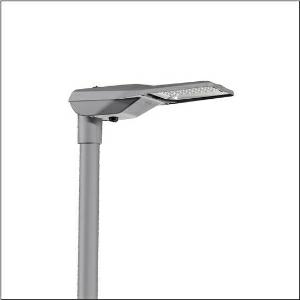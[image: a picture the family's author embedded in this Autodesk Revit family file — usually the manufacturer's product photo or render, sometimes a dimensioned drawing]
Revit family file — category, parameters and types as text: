
# Revit family: streetlight_sl_21_mini___st0_8a_5xe2c23t08hb_e0eb
name_source: partatom
category: Lighting Fixtures
units: mm (PartAtom-declared; Revit-internal decimal feet)

## family parameters
Cut with Voids When Loaded = No
Host = Face
Light Source = No
Part Type = Normal
Room Calculation Point = No
Round Connector Dimension = Use Diameter
Shared = No

## types (1)
- --- (1 x LED, 7490 lm, 66 W, 2200K)
    Apparent Load = 66 VA
    CIE Flux Codes = 38 75 97 100 100
    Color Rendering = 70
    Color Temperature = 2200K
    Default Elevation = 1800 mm
    Description = Streetlight SL 21 mini, mast luminaire, primary light control with lens, of PMMA, primary optical cover: cover, of toughened safety glass, transparent, light distribution: ST0.8a, light emission: direct distribution, primary light characteristic: asymmetric, installation type: side-entry, post-top, LED, High Power LED, rated luminous flux: 7.490lm, luminous efficacy: 114lm/W, light colour: 722, colour temperature: 2200K, control gear: D4i, control: overheat protection, constant luminous flux control, time-dependent luminous flux control, flexible luminous flux parameterisation, pre-setting: logarithmic dimming characteristic, mains connection: 220..240V, AC, 50/60Hz, start of lifetime: 66W, end of service life: 69W, reduction: 30W, luminaire housing, of diecast aluminium, powder-coated, Siteco® metallic grey (DB 702S), corrosivity category C5 mid according to DIN EN ISO 12944, please order mast flange separately, inclination adjustable: 0°, 5°, 10°, 15°, sealing non-destructively replaceable, multi-level sealing system, length: 628mm, width: 235mm, height: 110mm, mast flange for spigot size: 42mm (side-entry): 5XC10008XM4, 60/48mm (side-entry/post-top): 5XC10108XM2, 76/60mm (side-entry/post-top): 5XC10108XM1, mounting height: 4..8m, Smart Interface below and above, protection rating (complete): IP66, insulation class (complete): insulation class II (safety insulation), certification: CE, ENEC, ENEC+, VDE, impact resistance: IK10, permissible operating ambient temperature for outdoor applications: -40..+50°C, standard-compliant lighting for roads and squares, packaging unit: 1 piece

Light Distribution: ST0.8a
    Height = 110 mm
    Lamp = 1 x LED
    Lamp Light Flux = 7490 lm
    Lamp Power = 66 W
    Lamp count = 1
    Length = 625 mm
    Luminous efficacy = 113 lm/W
    Manufacturer = Siteco
    ModVariant = No
    Model = 5XE2C23T08HB
    Number of Poles = 1
    OnlyDefault = Yes
    Power Factor = 1
    Product Name = Streetlight SL 21 mini | ST0.8a
    Product group = mast luminaire | pylon top
    ProductGroupID = 6100
    Protection Class = Protection class II
    Protection Degree = IP 66
    RLX_Detail_Level = 1
    RLX_Emergency_Light_Flux = 0 lm
    RLX_Emergency_Type = 0
    RLX_Emergency_Type_DB = No
    RlxData = <blob elided: 26373 chars, md5=5c8eab5d>
    Socket = socket
    Standby Power = 0 W
    System Light Flux = 7490 lm
    System Power = 66 W
    Type Comments = factory setting: luminous flux: 100 % | dim-lin: 254 | 670 mA
    Type Image = l_1003514.jpg
    URL = http://relux.com
    VarID = @adj_206643
    Voltage = 0 V
    Weight = 0.00 kg
    Width = 234 mm

## geometry (parser evidence)
native form markers: Blend x4, Sweep x9
no freeform markers — native parametric forms only
